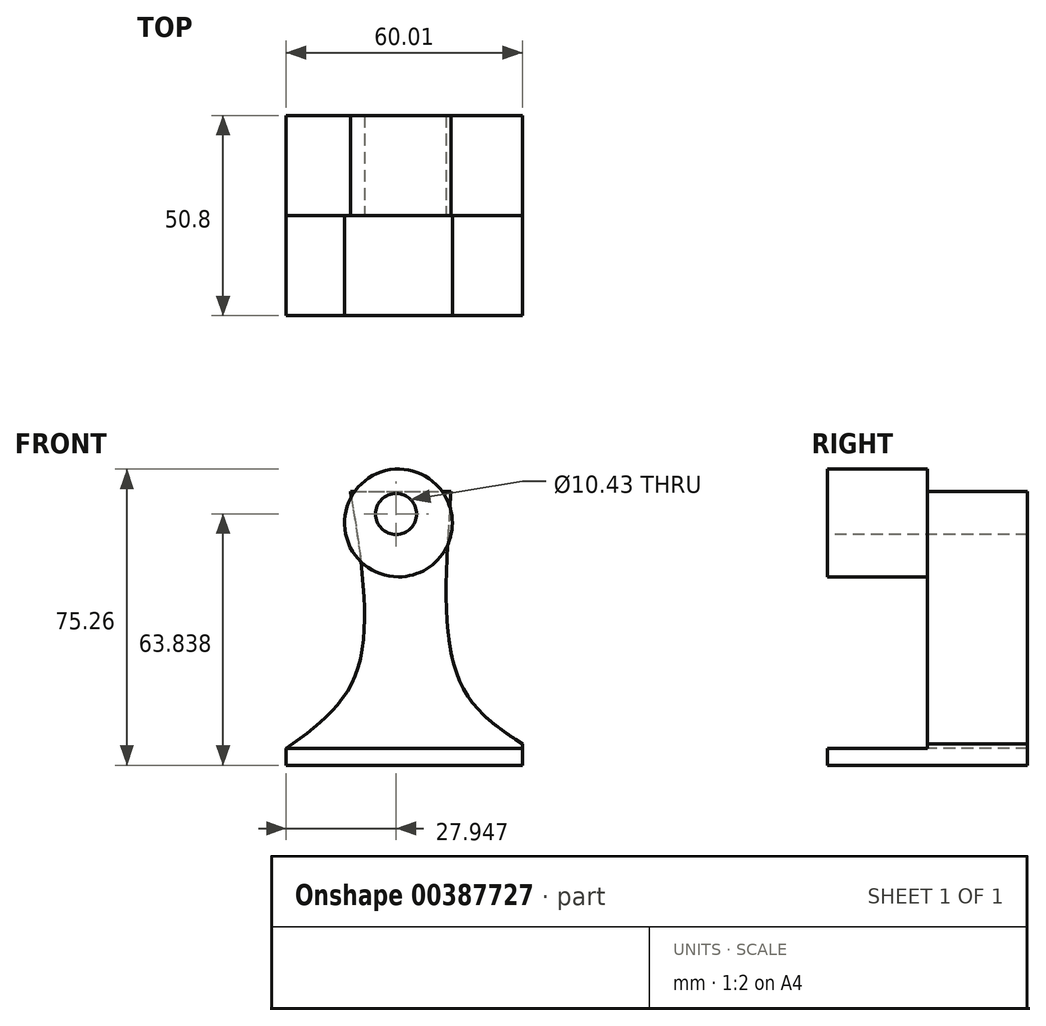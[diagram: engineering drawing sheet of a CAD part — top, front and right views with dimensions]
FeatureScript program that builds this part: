
annotation { "Feature Type Name" : "Feature", "Feature Type Description" : "" }
export const myFeature = defineFeature(function(context is Context, id is Id, definition is map)
    precondition{}
    {
        {
            var Q0;
            Q0=qCreatedBy(makeId("Front.planeOp"),FACE);
            var sketch = newSketch(context, id + "F0", { "sketchPlane" : qUnion([Q0])});
            skLineSegment(sketch, "E0", {"start": v(0, 0) * mm, "end": v(0, 69.51) * mm});
            skLineSegment(sketch, "E1", {"start": v(0, 69.51) * mm, "end": v(60, 69.51) * mm});
            skLineSegment(sketch, "E2", {"start": v(60, 69.51) * mm, "end": v(60, 0) * mm});
            skLineSegment(sketch, "E3", {"start": v(60, 0) * mm, "end": v(0, 0) * mm});
            skSolve(sketch);
        }
        {
            var Q0;
            Q0 = qSketchRegion(id + "F0", true);
            extrude(context, id + "F1", {"entities" : qUnion([Q0]), "depth" : 50.8 * mm});
        }
        {
            var Q0;
            Q0=makeQuery(id+"F1.opExtrude","CAP_FACE",FACE,{"disambiguationData":[OSD([sQuery(id+"F0.wireOp",EDGE,"E0"),sQuery(id+"F0.wireOp",EDGE,"E1"),sQuery(id+"F0.wireOp",EDGE,"E2"),sQuery(id+"F0.wireOp",EDGE,"E3")])],"isStart":false});
            var sketch = newSketch(context, id + "F2", { "sketchPlane" : qUnion([Q0])});
            skFitSpline(sketch, "E4", {"points": [v(16.31, 69.51) * mm, v(17.73, 23.27) * mm, v(0, 4.26) * mm], "startDerivative": vector(15.02, -91.36) * mm, "endDerivative": vector(-50.79, -36.54) * mm});
            skFitSpline(sketch, "E5", {"points": [v(41.85, 69.51) * mm, v(44.12, 21.28) * mm, v(60, 5.4) * mm], "startDerivative": vector(-6.7, -93.6) * mm, "endDerivative": vector(46.35, -30.67) * mm});
            skSolve(sketch);
        }
        {
            var Q0;
            {var subQ0=sQuery(id+"F2.wireOp",EDGE,"E5");Q0=makeQuery(id+"F2.imprint","IMPRINT",FACE,{"disambiguationData":[TD([[makeQuery(id+"F2.imprint","IMPRINT",EDGE,{"derivedFrom":subQ0}),1.0]])]});}
            var Q1;
            {var subQ0=sQuery(id+"F2.wireOp",EDGE,"E4");Q1=makeQuery(id+"F2.imprint","IMPRINT",FACE,{"disambiguationData":[TD([[makeQuery(id+"F2.imprint","IMPRINT",EDGE,{"derivedFrom":subQ0}),-1.0]])]});}
            extrude(context, id + "F3", {"entities" : qUnion([Q0, Q1]), "operationType" : NewBodyOperationType.REMOVE, "oppositeDirection" : true, "depth" : 50.8 * mm});
        }
        {
            var Q0;
            Q0=makeQuery(id+"F1.opExtrude","CAP_FACE",FACE,{"disambiguationData":[OSD([sQuery(id+"F0.wireOp",EDGE,"E0"),sQuery(id+"F0.wireOp",EDGE,"E1"),sQuery(id+"F0.wireOp",EDGE,"E2"),sQuery(id+"F0.wireOp",EDGE,"E3")])],"isStart":false});
            var sketch = newSketch(context, id + "F4", { "sketchPlane" : qUnion([Q0])});
            skLineSegment(sketch, "E6", {"start": v(0, 4.26) * mm, "end": v(60, 4.26) * mm});
            skSolve(sketch);
        }
        {
            var Q0;
            {var subQ1=sQuery(id+"F4.wireOp",EDGE,"E6");Q0=makeQuery(id+"F4.imprint","IMPRINT",FACE,{"disambiguationData":[TD([[makeQuery(id+"F4.imprint","IMPRINT",EDGE,{"derivedFrom":subQ1}),1.0]])]});}
            extrude(context, id + "F5", {"entities" : qUnion([Q0]), "operationType" : NewBodyOperationType.REMOVE, "oppositeDirection" : true, "depth" : 25.4 * mm});
        }
        {
            var Q0;
            Q0=makeQuery(id+"F5.boolean.opBoolean","COPY",FACE,{"derivedFrom":makeQuery(id+"F5.opExtrude","CAP_FACE",FACE,{"disambiguationData":[OSD([sQuery(id+"F0.wireOp",EDGE,"E1"),sQuery(id+"F0.wireOp",EDGE,"E2"),sQuery(id+"F2.wireOp",EDGE,"E4"),sQuery(id+"F2.wireOp",EDGE,"E5"),sQuery(id+"F4.wireOp",EDGE,"E6")])],"isStart":false})});
            var sketch = newSketch(context, id + "F6", { "sketchPlane" : qUnion([Q0])});
            skCircle(sketch, "E7", {"center": v(28.51, 61.57) * mm, "radius": 13.7 * mm});
            skSolve(sketch);
        }
        {
            var Q0;
            Q0 = qSketchRegion(id + "F6", true);
            extrude(context, id + "F7", {"entities" : qUnion([Q0]), "operationType" : NewBodyOperationType.ADD, "depth" : 25.4 * mm});
        }
        {
            var Q0;
            Q0=makeQuery(id+"F7.opExtrude","CAP_FACE",FACE,{"disambiguationData":[OSD([sQuery(id+"F6.wireOp",EDGE,"E7")])],"isStart":false});
            var sketch = newSketch(context, id + "F8", { "sketchPlane" : qUnion([Q0])});
            skCircle(sketch, "E8", {"center": v(27.95, 63.84) * mm, "radius": 5.22 * mm});
            skSolve(sketch);
        }
        {
            var Q0;
            Q0=makeQuery(id+"F8.imprint","IMPRINT",FACE,{"disambiguationData":[TD([[makeQuery(id+"F8.imprint","IMPRINT",EDGE,{"derivedFrom":sQuery(id+"F8.wireOp",EDGE,"E8")}),1.0]])]});
            extrude(context, id + "F9", {"entities" : qUnion([Q0]), "operationType" : NewBodyOperationType.REMOVE, "oppositeDirection" : true, "depth" : 50.8 * mm});
        }
    });
